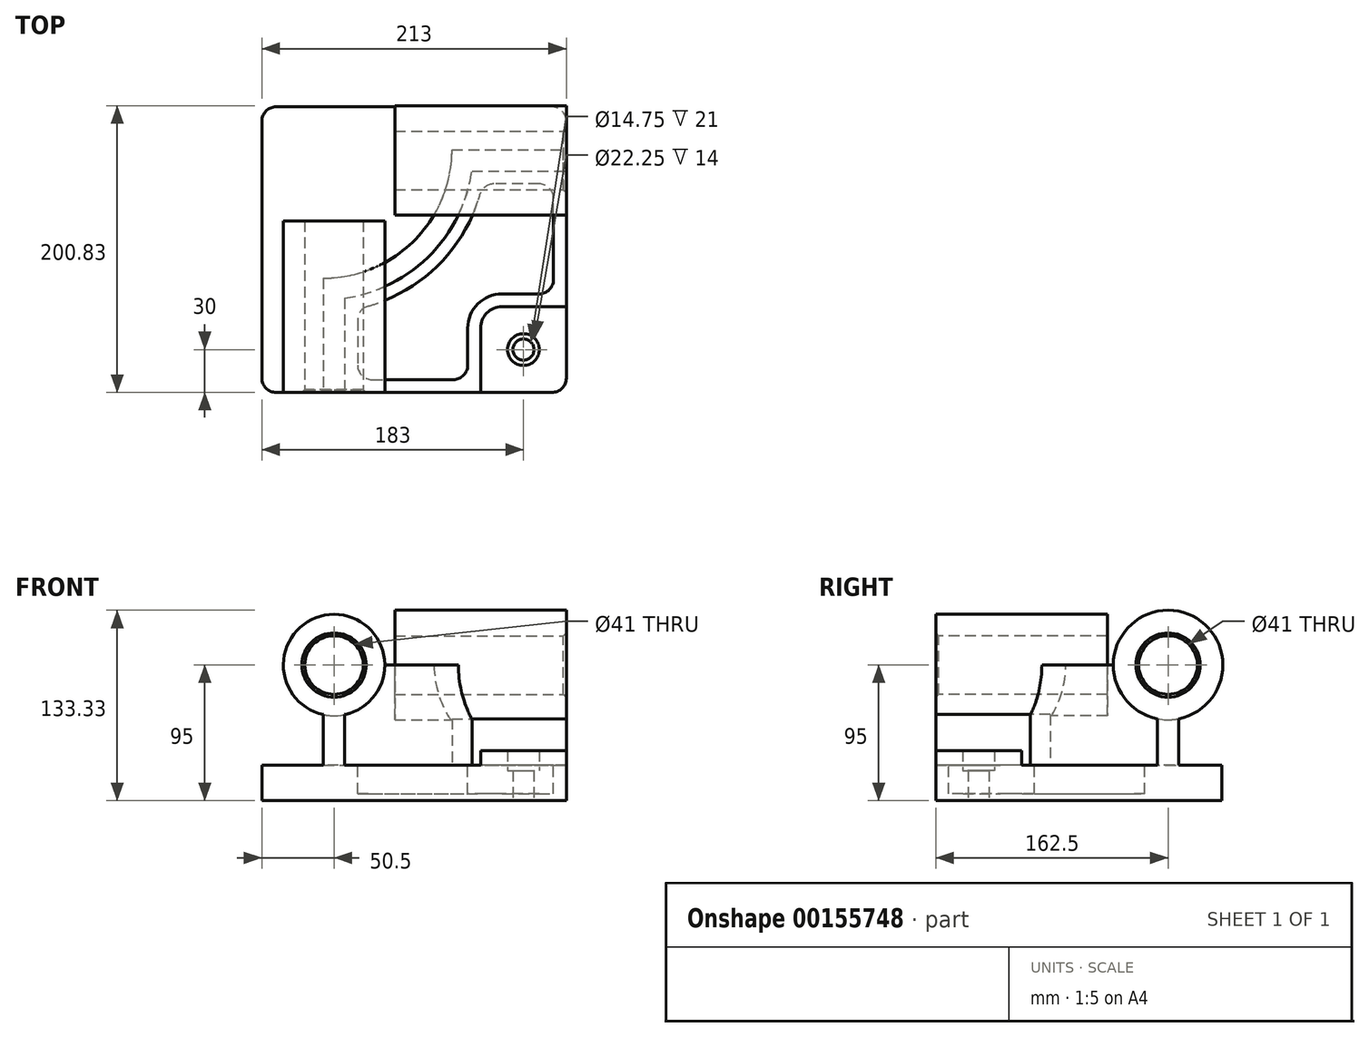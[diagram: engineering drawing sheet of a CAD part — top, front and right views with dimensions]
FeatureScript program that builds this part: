
annotation { "Feature Type Name" : "Feature", "Feature Type Description" : "" }
export const myFeature = defineFeature(function(context is Context, id is Id, definition is map)
    precondition{}
    {
        {
            var Q0;
            Q0=qCreatedBy(makeId("Top.planeOp"),FACE);
            var sketch = newSketch(context, id + "F0", { "sketchPlane" : qUnion([Q0])});
            skLineSegment(sketch, "E0.bottom", {"start": v(0, 0) * mm, "end": v(-213, 0) * mm});
            skLineSegment(sketch, "E0.top", {"start": v(0, -200) * mm, "end": v(-213, -200) * mm});
            skLineSegment(sketch, "E0.left", {"start": v(0, 0) * mm, "end": v(0, -200) * mm});
            skLineSegment(sketch, "E0.right", {"start": v(-213, 0) * mm, "end": v(-213, -200) * mm});
            skSolve(sketch);
        }
        {
            var Q0;
            Q0=makeQuery(id+"F0.imprint","IMPRINT",FACE,{"disambiguationData":[TD([[makeQuery(id+"F0.imprint","IMPRINT",EDGE,{"derivedFrom":sQuery(id+"F0.wireOp",EDGE,"E0.bottom")}),1.0]])]});
            extrude(context, id + "F1", {"entities" : qUnion([Q0]), "depth" : 25 * mm});
        }
        {
            var Q0;
            Q0=qCreatedBy(makeId("Top.planeOp"),FACE);
            cPlane(context, id + "F2", {"entities" : qUnion([Q0]), "cplaneType" : CPlaneType.OFFSET, "offset" : 95 * mm, "width" : 150 * mm, "height" : 150 * mm});
        }
        {
            var Q0;
            Q0=qCreatedBy(makeId("Right.planeOp"),FACE);
            var sketch = newSketch(context, id + "F3", { "sketchPlane" : qUnion([Q0])});
            skLineSegment(sketch, "E1.bottom", {"start": v(-30, 25) * mm, "end": v(-45, 25) * mm});
            skLineSegment(sketch, "E1.left", {"start": v(-30, 25) * mm, "end": v(-30, 57.4) * mm});
            skLineSegment(sketch, "E1.right", {"start": v(-45, 25) * mm, "end": v(-45, 57.4) * mm});
            skPoint(sketch, "E2", {"position": v(-37.5, 25) * mm});
            skLineSegment(sketch, "E3", {"start": v(-37.5, 25) * mm, "end": v(-37.5, 95) * mm, "construction": true});
            skArc(sketch, "E4", {"start": v(-30, 57.4) * mm, "mid": v(-37.5, 133.33) * mm, "end": v(-45, 57.4) * mm});
            skCircle(sketch, "E5", {"center": v(-37.5, 95) * mm, "radius": 20.5 * mm});
            skSolve(sketch);
        }
        {
            var Q0;
            Q0=makeQuery(id+"F3.imprint","IMPRINT",FACE,{"disambiguationData":[TD([[makeQuery(id+"F3.imprint","IMPRINT",EDGE,{"derivedFrom":sQuery(id+"F3.wireOp",EDGE,"E1.bottom")}),-1.0]])]});
            extrude(context, id + "F4", {"entities" : qUnion([Q0]), "operationType" : NewBodyOperationType.ADD, "oppositeDirection" : true, "depth" : 120 * mm});
        }
        {
            var Q0;
            Q0=makeQuery(id+"F1.opExtrude","SWEPT_FACE",FACE,{"disambiguationData":[OSD([sQuery(id+"F0.wireOp",EDGE,"E0.top")])]});
            var sketch = newSketch(context, id + "F5", { "sketchPlane" : qUnion([Q0])});
            skLineSegment(sketch, "E6.bottom", {"start": v(-170, 25) * mm, "end": v(-155, 25) * mm});
            skLineSegment(sketch, "E6.left", {"start": v(-170, 25) * mm, "end": v(-170, 60.3) * mm});
            skLineSegment(sketch, "E6.right", {"start": v(-155, 25) * mm, "end": v(-155, 60.3) * mm});
            skPoint(sketch, "E7", {"position": v(-162.5, 25) * mm});
            skLineSegment(sketch, "E8", {"start": v(-162.5, 25) * mm, "end": v(-162.5, 95) * mm, "construction": true});
            skArc(sketch, "E9", {"start": v(-155, 60.3) * mm, "mid": v(-162.5, 130.5) * mm, "end": v(-170, 60.3) * mm});
            skCircle(sketch, "E10", {"center": v(-162.5, 95) * mm, "radius": 20.5 * mm});
            skSolve(sketch);
        }
        {
            var Q0;
            Q0=makeQuery(id+"F5.imprint","IMPRINT",FACE,{"disambiguationData":[TD([[makeQuery(id+"F5.imprint","IMPRINT",EDGE,{"derivedFrom":sQuery(id+"F5.wireOp",EDGE,"E6.bottom")}),-1.0]])]});
            extrude(context, id + "F6", {"entities" : qUnion([Q0]), "operationType" : NewBodyOperationType.ADD, "oppositeDirection" : true, "depth" : 120 * mm});
        }
        {
            var Q0;
            Q0=makeQuery(id+"F1.opExtrude","CAP_FACE",FACE,{"disambiguationData":[OSD([sQuery(id+"F0.wireOp",EDGE,"E0.bottom"),sQuery(id+"F0.wireOp",EDGE,"E0.top"),sQuery(id+"F0.wireOp",EDGE,"E0.left"),sQuery(id+"F0.wireOp",EDGE,"E0.right")])],"isStart":false});
            var sketch = newSketch(context, id + "F7", { "sketchPlane" : qUnion([Q0])});
            skLineSegment(sketch, "E11", {"start": v(-80, -30) * mm, "end": v(-80, 39.63) * mm, "construction": true});
            skLineSegment(sketch, "E12", {"start": v(-170, -120) * mm, "end": v(-209.61, -120) * mm, "construction": true});
            skArc(sketch, "E13", {"start": v(-170, -120) * mm, "mid": v(-106.36, -93.64) * mm, "end": v(-80, -30) * mm});
            skArc(sketch, "E14.0", {"start": v(-170, -135) * mm, "mid": v(-95.75, -104.25) * mm, "end": v(-65, -30) * mm});
            skLineSegment(sketch, "E15", {"start": v(-170, -120) * mm, "end": v(-170, -135) * mm});
            skLineSegment(sketch, "E16", {"start": v(-80, -30) * mm, "end": v(-65, -30) * mm});
            skSolve(sketch);
        }
        {
            var Q0;
            Q0 = qSketchRegion(id + "F7", true);
            var Q1;
            Q1=qCreatedBy(id+"F2.planeOp",FACE);
            extrude(context, id + "F8", {"entities" : qUnion([Q0]), "operationType" : NewBodyOperationType.ADD, "endBound" : BoundingType.UP_TO_SURFACE, "endBoundEntityFace" : qUnion([Q1]), "depth" : 25 * mm});
        }
        {
            var Q0;
            Q0=makeQuery(id+"F4.opExtrude","CAP_FACE",FACE,{"disambiguationData":[OSD([sQuery(id+"F3.wireOp",EDGE,"E1.bottom"),sQuery(id+"F3.wireOp",EDGE,"E1.left"),sQuery(id+"F3.wireOp",EDGE,"E1.right"),sQuery(id+"F3.wireOp",EDGE,"E4"),sQuery(id+"F3.wireOp",EDGE,"E5")])],"isStart":false});
            var sketch = newSketch(context, id + "F9", { "sketchPlane" : qUnion([Q0])});
            skLineSegment(sketch, "E17.0.0", {"start": v(30, 57.4) * mm, "end": v(30, 25) * mm});
            skLineSegment(sketch, "E17.0.1", {"start": v(30, 25) * mm, "end": v(45, 25) * mm});
            skLineSegment(sketch, "E17.0.2", {"start": v(45, 25) * mm, "end": v(45, 57.4) * mm});
            skArc(sketch, "E18", {"start": v(30, 57.4) * mm, "mid": v(37.5, 56.67) * mm, "end": v(45, 57.4) * mm});
            skSolve(sketch);
        }
        {
            var Q0;
            Q0=makeQuery(id+"F9.imprint","IMPRINT",FACE,{"disambiguationData":[TD([[makeQuery(id+"F9.imprint","IMPRINT",EDGE,{"derivedFrom":sQuery(id+"F9.wireOp",EDGE,"E17.0.0")}),-1.0]])]});
            var Q1;
            Q1=makeQuery(id+"F8.boolean.opBoolean","SPLIT",FACE,{"disambiguationData":[TD([makeQuery(id+"F4.opExtrude","SWEPT_FACE",FACE,{"disambiguationData":[OSD([sQuery(id+"F3.wireOp",EDGE,"E5")])]})])],"derivedFrom":makeQuery(id+"F8.opExtrude","SWEPT_FACE",FACE,{"disambiguationData":[OSD([sQuery(id+"F7.wireOp",EDGE,"E13")])]})});
            extrude(context, id + "F10", {"entities" : qUnion([Q0]), "operationType" : NewBodyOperationType.REMOVE, "endBound" : BoundingType.UP_TO_SURFACE, "oppositeDirection" : true, "endBoundEntityFace" : qUnion([Q1]), "depth" : 25 * mm});
        }
        {
            var Q0;
            Q0=makeQuery(id+"F6.opExtrude","CAP_FACE",FACE,{"disambiguationData":[OSD([sQuery(id+"F5.wireOp",EDGE,"E6.bottom"),sQuery(id+"F5.wireOp",EDGE,"E6.left"),sQuery(id+"F5.wireOp",EDGE,"E6.right"),sQuery(id+"F5.wireOp",EDGE,"E9"),sQuery(id+"F5.wireOp",EDGE,"E10")])],"isStart":false});
            var sketch = newSketch(context, id + "F11", { "sketchPlane" : qUnion([Q0])});
            skLineSegment(sketch, "E19.0.0", {"start": v(155, 25) * mm, "end": v(170, 25) * mm});
            skLineSegment(sketch, "E19.0.1", {"start": v(170, 25) * mm, "end": v(170, 60.3) * mm});
            skLineSegment(sketch, "E19.0.3", {"start": v(155, 60.3) * mm, "end": v(155, 25) * mm});
            skArc(sketch, "E20", {"start": v(155, 60.3) * mm, "mid": v(162.5, 59.5) * mm, "end": v(170, 60.3) * mm});
            skSolve(sketch);
        }
        {
            var Q0;
            Q0 = qSketchRegion(id + "F11", true);
            var Q1;
            Q1=makeQuery(id+"F8.boolean.opBoolean","SPLIT",FACE,{"disambiguationData":[TD([makeQuery(id+"F6.opExtrude","SWEPT_FACE",FACE,{"disambiguationData":[OSD([sQuery(id+"F5.wireOp",EDGE,"E10")])]})])],"derivedFrom":makeQuery(id+"F8.opExtrude","SWEPT_FACE",FACE,{"disambiguationData":[OSD([sQuery(id+"F7.wireOp",EDGE,"E13")])]})});
            extrude(context, id + "F12", {"entities" : qUnion([Q0]), "operationType" : NewBodyOperationType.REMOVE, "endBound" : BoundingType.UP_TO_SURFACE, "oppositeDirection" : true, "endBoundEntityFace" : qUnion([Q1]), "depth" : 25 * mm});
        }
        {
            var Q0;
            Q0=makeQuery(id+"F4.boolean.opBoolean","MERGE",FACE,{"derivedFrom":[makeQuery(id+"F1.opExtrude","SWEPT_FACE",FACE,{"disambiguationData":[OSD([sQuery(id+"F0.wireOp",EDGE,"E0.left")])]}),makeQuery(id+"F4.opExtrude","CAP_FACE",FACE,{"disambiguationData":[OSD([sQuery(id+"F3.wireOp",EDGE,"E1.bottom"),sQuery(id+"F3.wireOp",EDGE,"E1.left"),sQuery(id+"F3.wireOp",EDGE,"E1.right"),sQuery(id+"F3.wireOp",EDGE,"E4"),sQuery(id+"F3.wireOp",EDGE,"E5")])],"isStart":true})]});
            var sketch = newSketch(context, id + "F13", { "sketchPlane" : qUnion([Q0])});
            skCircle(sketch, "E21.0", {"center": v(-37.5, 95) * mm, "radius": 20.5 * mm});
            skSolve(sketch);
        }
        {
            var Q0;
            Q0 = qSketchRegion(id + "F13", true);
            extrude(context, id + "F14", {"entities" : qUnion([Q0]), "operationType" : NewBodyOperationType.REMOVE, "endBound" : BoundingType.THROUGH_ALL, "oppositeDirection" : true, "depth" : 25 * mm});
        }
        {
            var Q0;
            Q0=makeQuery(id+"F6.boolean.opBoolean","MERGE",FACE,{"derivedFrom":[makeQuery(id+"F1.opExtrude","SWEPT_FACE",FACE,{"disambiguationData":[OSD([sQuery(id+"F0.wireOp",EDGE,"E0.top")])]}),makeQuery(id+"F6.opExtrude","CAP_FACE",FACE,{"disambiguationData":[OSD([sQuery(id+"F5.wireOp",EDGE,"E6.bottom"),sQuery(id+"F5.wireOp",EDGE,"E6.left"),sQuery(id+"F5.wireOp",EDGE,"E6.right"),sQuery(id+"F5.wireOp",EDGE,"E9"),sQuery(id+"F5.wireOp",EDGE,"E10")])],"isStart":true})]});
            var sketch = newSketch(context, id + "F15", { "sketchPlane" : qUnion([Q0])});
            skCircle(sketch, "E22.0", {"center": v(-162.5, 95) * mm, "radius": 20.5 * mm});
            skSolve(sketch);
        }
        {
            var Q0;
            Q0 = qSketchRegion(id + "F15", true);
            extrude(context, id + "F16", {"entities" : qUnion([Q0]), "operationType" : NewBodyOperationType.REMOVE, "endBound" : BoundingType.THROUGH_ALL, "oppositeDirection" : true, "depth" : 25 * mm});
        }
        {
            var Q0;
            {var subQ1=sQuery(id+"F0.wireOp",EDGE,"E0.left");var subQ2=sQuery(id+"F0.wireOp",EDGE,"E0.top");Q0=makeQuery(id+"F8.boolean.opBoolean","SPLIT",FACE,{"disambiguationData":[TD([makeQuery(id+"F8.opExtrude","SWEPT_FACE",FACE,{"disambiguationData":[OSD([sQuery(id+"F7.wireOp",EDGE,"E14.0")])]})])],"derivedFrom":makeQuery(id+"F1.opExtrude","CAP_FACE",FACE,{"disambiguationData":[OSD([sQuery(id+"F0.wireOp",EDGE,"E0.bottom"),subQ2,subQ1,sQuery(id+"F0.wireOp",EDGE,"E0.right")])],"isStart":false})});}
            var sketch = newSketch(context, id + "F17", { "sketchPlane" : qUnion([Q0])});
            skLineSegment(sketch, "E23.bottom", {"start": v(0, -200) * mm, "end": v(-60, -200) * mm});
            skLineSegment(sketch, "E23.top", {"start": v(0, -140) * mm, "end": v(-60, -140) * mm});
            skLineSegment(sketch, "E23.left", {"start": v(0, -200) * mm, "end": v(0, -140) * mm});
            skLineSegment(sketch, "E23.right", {"start": v(-60, -200) * mm, "end": v(-60, -140) * mm});
            skSolve(sketch);
        }
        {
            var Q0;
            Q0 = qSketchRegion(id + "F17", true);
            extrude(context, id + "F18", {"entities" : qUnion([Q0]), "operationType" : NewBodyOperationType.ADD, "depth" : 10 * mm});
        }
        {
            var Q0;
            {var subQ1=sQuery(id+"F0.wireOp",EDGE,"E0.left");var subQ2=sQuery(id+"F0.wireOp",EDGE,"E0.top");Q0=makeQuery(id+"F8.boolean.opBoolean","SPLIT",FACE,{"disambiguationData":[TD([makeQuery(id+"F8.opExtrude","SWEPT_FACE",FACE,{"disambiguationData":[OSD([sQuery(id+"F7.wireOp",EDGE,"E14.0")])]})])],"derivedFrom":makeQuery(id+"F1.opExtrude","CAP_FACE",FACE,{"disambiguationData":[OSD([sQuery(id+"F0.wireOp",EDGE,"E0.bottom"),subQ2,subQ1,sQuery(id+"F0.wireOp",EDGE,"E0.right")])],"isStart":false})});}
            var sketch = newSketch(context, id + "F19", { "sketchPlane" : qUnion([Q0])});
            skLineSegment(sketch, "E24.0", {"start": v(-146, -141.45) * mm, "end": v(-146, -191) * mm});
            skArc(sketch, "E24.1", {"start": v(-58.55, -54) * mm, "mid": v(-89.39, -110.61) * mm, "end": v(-146, -141.45) * mm});
            skLineSegment(sketch, "E24.2", {"start": v(-69, -191) * mm, "end": v(-69, -131) * mm});
            skLineSegment(sketch, "E24.3", {"start": v(-69, -131) * mm, "end": v(-9, -131) * mm});
            skLineSegment(sketch, "E24.4", {"start": v(-9, -131) * mm, "end": v(-9, -54) * mm});
            skLineSegment(sketch, "E24.5", {"start": v(-146, -191) * mm, "end": v(-69, -191) * mm});
            skLineSegment(sketch, "E24.6", {"start": v(-9, -54) * mm, "end": v(-58.55, -54) * mm});
            skSolve(sketch);
        }
        {
            var Q0;
            Q0 = qSketchRegion(id + "F19", true);
            extrude(context, id + "F20", {"entities" : qUnion([Q0]), "operationType" : NewBodyOperationType.REMOVE, "oppositeDirection" : true, "depth" : 20 * mm});
        }
        {
            var Q0;
            Q0=makeQuery(id+"F20.boolean.opBoolean","COPY",EDGE,{"derivedFrom":makeQuery(id+"F20.opExtrude","SWEPT_EDGE",EDGE,{"disambiguationData":[OSD([sQuery(id+"F19.wireOp",EDGE,"E24.0"),sQuery(id+"F19.wireOp",EDGE,"E24.1")])]})});
            var Q1;
            Q1=makeQuery(id+"F20.boolean.opBoolean","COPY",EDGE,{"derivedFrom":makeQuery(id+"F20.opExtrude","SWEPT_EDGE",EDGE,{"disambiguationData":[OSD([sQuery(id+"F19.wireOp",EDGE,"E24.1"),sQuery(id+"F19.wireOp",EDGE,"E24.6")])]})});
            var Q2;
            Q2=makeQuery(id+"F20.boolean.opBoolean","COPY",EDGE,{"derivedFrom":makeQuery(id+"F20.opExtrude","SWEPT_EDGE",EDGE,{"disambiguationData":[OSD([sQuery(id+"F19.wireOp",EDGE,"E24.0"),sQuery(id+"F19.wireOp",EDGE,"E24.5")])]})});
            var Q3;
            Q3=makeQuery(id+"F20.boolean.opBoolean","COPY",EDGE,{"derivedFrom":makeQuery(id+"F20.opExtrude","SWEPT_EDGE",EDGE,{"disambiguationData":[OSD([sQuery(id+"F19.wireOp",EDGE,"E24.2"),sQuery(id+"F19.wireOp",EDGE,"E24.5")])]})});
            var Q4;
            Q4=makeQuery(id+"F20.boolean.opBoolean","COPY",EDGE,{"derivedFrom":makeQuery(id+"F20.opExtrude","SWEPT_EDGE",EDGE,{"disambiguationData":[OSD([sQuery(id+"F19.wireOp",EDGE,"E24.3"),sQuery(id+"F19.wireOp",EDGE,"E24.4")])]})});
            var Q5;
            Q5=makeQuery(id+"F20.boolean.opBoolean","COPY",EDGE,{"derivedFrom":makeQuery(id+"F20.opExtrude","SWEPT_EDGE",EDGE,{"disambiguationData":[OSD([sQuery(id+"F19.wireOp",EDGE,"E24.4"),sQuery(id+"F19.wireOp",EDGE,"E24.6")])]})});
            fillet(context, id + "F21", {"entities" : qUnion([Q0, Q1, Q2, Q3, Q4, Q5]), "radius" : 10 * mm, "tangentPropagation" : true, "allowEdgeOverflow" : false});
        }
        {
            var Q0;
            Q0=makeQuery(id+"F18.opExtrude","SWEPT_EDGE",EDGE,{"disambiguationData":[OSD([sQuery(id+"F17.wireOp",EDGE,"E23.top"),sQuery(id+"F17.wireOp",EDGE,"E23.right")])]});
            fillet(context, id + "F22", {"entities" : qUnion([Q0]), "radius" : 15 * mm, "tangentPropagation" : true, "allowEdgeOverflow" : false});
        }
        {
            var Q0;
            Q0=makeQuery(id+"F1.opExtrude","SWEPT_EDGE",EDGE,{"disambiguationData":[OSD([sQuery(id+"F0.wireOp",EDGE,"E0.top"),sQuery(id+"F0.wireOp",EDGE,"E0.right")])]});
            var Q1;
            Q1=makeQuery(id+"F18.boolean.opBoolean","MERGE",EDGE,{"derivedFrom":[makeQuery(id+"F1.opExtrude","SWEPT_EDGE",EDGE,{"disambiguationData":[OSD([sQuery(id+"F0.wireOp",EDGE,"E0.top"),sQuery(id+"F0.wireOp",EDGE,"E0.left")])]}),makeQuery(id+"F18.opExtrude","SWEPT_EDGE",EDGE,{"disambiguationData":[OSD([sQuery(id+"F17.wireOp",EDGE,"E23.bottom"),sQuery(id+"F17.wireOp",EDGE,"E23.left")])]})]});
            var Q2;
            Q2=makeQuery(id+"F1.opExtrude","SWEPT_EDGE",EDGE,{"disambiguationData":[OSD([sQuery(id+"F0.wireOp",EDGE,"E0.bottom"),sQuery(id+"F0.wireOp",EDGE,"E0.right")])]});
            var Q3;
            Q3=makeQuery(id+"F1.opExtrude","SWEPT_EDGE",EDGE,{"disambiguationData":[OSD([sQuery(id+"F0.wireOp",EDGE,"E0.bottom"),sQuery(id+"F0.wireOp",EDGE,"E0.left")])]});
            fillet(context, id + "F23", {"entities" : qUnion([Q0, Q1, Q2, Q3]), "radius" : 10 * mm, "tangentPropagation" : true, "allowEdgeOverflow" : false});
        }
        {
            var Q0;
            Q0=makeQuery(id+"F6.opExtrude","CAP_EDGE",EDGE,{"disambiguationData":[OSD([sQuery(id+"F5.wireOp",EDGE,"E10")])],"isStart":true});
            var Q1;
            Q1=makeQuery(id+"F4.opExtrude","CAP_EDGE",EDGE,{"disambiguationData":[OSD([sQuery(id+"F3.wireOp",EDGE,"E5")])],"isStart":false});
            var Q2;
            Q2=makeQuery(id+"F6.opExtrude","CAP_EDGE",EDGE,{"disambiguationData":[OSD([sQuery(id+"F5.wireOp",EDGE,"E10")])],"isStart":false});
            var Q3;
            Q3=makeQuery(id+"F4.opExtrude","CAP_EDGE",EDGE,{"disambiguationData":[OSD([sQuery(id+"F3.wireOp",EDGE,"E5")])],"isStart":true});
            chamfer(context, id + "F24", {"entities" : qUnion([Q0, Q1, Q2, Q3]), "width" : 2 * mm, "tangentPropagation" : true});
        }
        {
            var Q0;
            Q0=makeQuery(id+"F18.opExtrude","CAP_FACE",FACE,{"disambiguationData":[OSD([sQuery(id+"F17.wireOp",EDGE,"E23.bottom"),sQuery(id+"F17.wireOp",EDGE,"E23.top"),sQuery(id+"F17.wireOp",EDGE,"E23.left"),sQuery(id+"F17.wireOp",EDGE,"E23.right")])],"isStart":false});
            var sketch = newSketch(context, id + "F25", { "sketchPlane" : qUnion([Q0])});
            skPoint(sketch, "E25", {"position": v(-30, -170) * mm});
            skSolve(sketch);
        }
        {
            var Q0;
            Q0=sQuery(id+"F25.wireOp",VERTEX,"E25");
            var Q1;
            Q1=makeQuery(id+"F1.opExtrude","SWEPT_BODY",BODY,{"disambiguationData":[OSD([sQuery(id+"F0.wireOp",EDGE,"E0.bottom"),sQuery(id+"F0.wireOp",EDGE,"E0.top"),sQuery(id+"F0.wireOp",EDGE,"E0.left"),sQuery(id+"F0.wireOp",EDGE,"E0.right")])]});
            hole(context, id + "F26", {"style" : HoleStyle.C_BORE, "endStyle" : HoleEndStyle.THROUGH, "standardTappedOrClearance" : lookupTablePath({ "standard" : "ISO", "fit" : "Close", "size" : "M14", "type" : "Clearance" }), "standardBlindInLast" : lookupTablePath({ "fit" : "Close", "standard" : "ISO", "size" : "M14", "type" : "Clearance" }), "holeDiameter" : 14.75 * mm, "cBoreDiameter" : 22.25 * mm, "cBoreDepth" : 14 * mm, "tappedDepth" : 12 * mm, "tapClearance" : 3, "locations" : qUnion([Q0]), "scope" : qUnion([Q1])});
        }
        {
            var Q0;
            {var subQ1=sQuery(id+"F0.wireOp",EDGE,"E0.left");var subQ2=sQuery(id+"F0.wireOp",EDGE,"E0.top");Q0=makeQuery(id+"F8.boolean.opBoolean","SPLIT",FACE,{"disambiguationData":[TD([makeQuery(id+"F8.opExtrude","SWEPT_FACE",FACE,{"disambiguationData":[OSD([sQuery(id+"F7.wireOp",EDGE,"E14.0")])]})])],"derivedFrom":makeQuery(id+"F1.opExtrude","CAP_FACE",FACE,{"disambiguationData":[OSD([sQuery(id+"F0.wireOp",EDGE,"E0.bottom"),subQ2,subQ1,sQuery(id+"F0.wireOp",EDGE,"E0.right")])],"isStart":false})});}
            var sketch = newSketch(context, id + "F27", { "sketchPlane" : qUnion([Q0])});
            skArc(sketch, "E26.0", {"start": v(-69, -155) * mm, "mid": v(-61.97, -138.03) * mm, "end": v(-45, -131) * mm});
            skLineSegment(sketch, "E27.0", {"start": v(-69, -155) * mm, "end": v(-69, -131) * mm});
            skLineSegment(sketch, "E28.0", {"start": v(-69, -131) * mm, "end": v(-45, -131) * mm});
            skPoint(sketch, "E29.orphan", {"position": v(-19, -131) * mm});
            skPoint(sketch, "E30.orphan", {"position": v(-69, -181) * mm});
            skSolve(sketch);
        }
        {
            var Q0;
            Q0 = qSketchRegion(id + "F27", true);
            var Q1;
            Q1=makeQuery(id+"F20.boolean.opBoolean","COPY",FACE,{"derivedFrom":makeQuery(id+"F20.opExtrude","CAP_FACE",FACE,{"disambiguationData":[OSD([sQuery(id+"F19.wireOp",EDGE,"E24.0"),sQuery(id+"F19.wireOp",EDGE,"E24.1"),sQuery(id+"F19.wireOp",EDGE,"E24.2"),sQuery(id+"F19.wireOp",EDGE,"E24.3"),sQuery(id+"F19.wireOp",EDGE,"E24.4"),sQuery(id+"F19.wireOp",EDGE,"E24.5"),sQuery(id+"F19.wireOp",EDGE,"E24.6")])],"isStart":false})});
            extrude(context, id + "F28", {"entities" : qUnion([Q0]), "operationType" : NewBodyOperationType.REMOVE, "endBound" : BoundingType.UP_TO_SURFACE, "oppositeDirection" : true, "endBoundEntityFace" : qUnion([Q1]), "depth" : 25 * mm});
        }
    });
